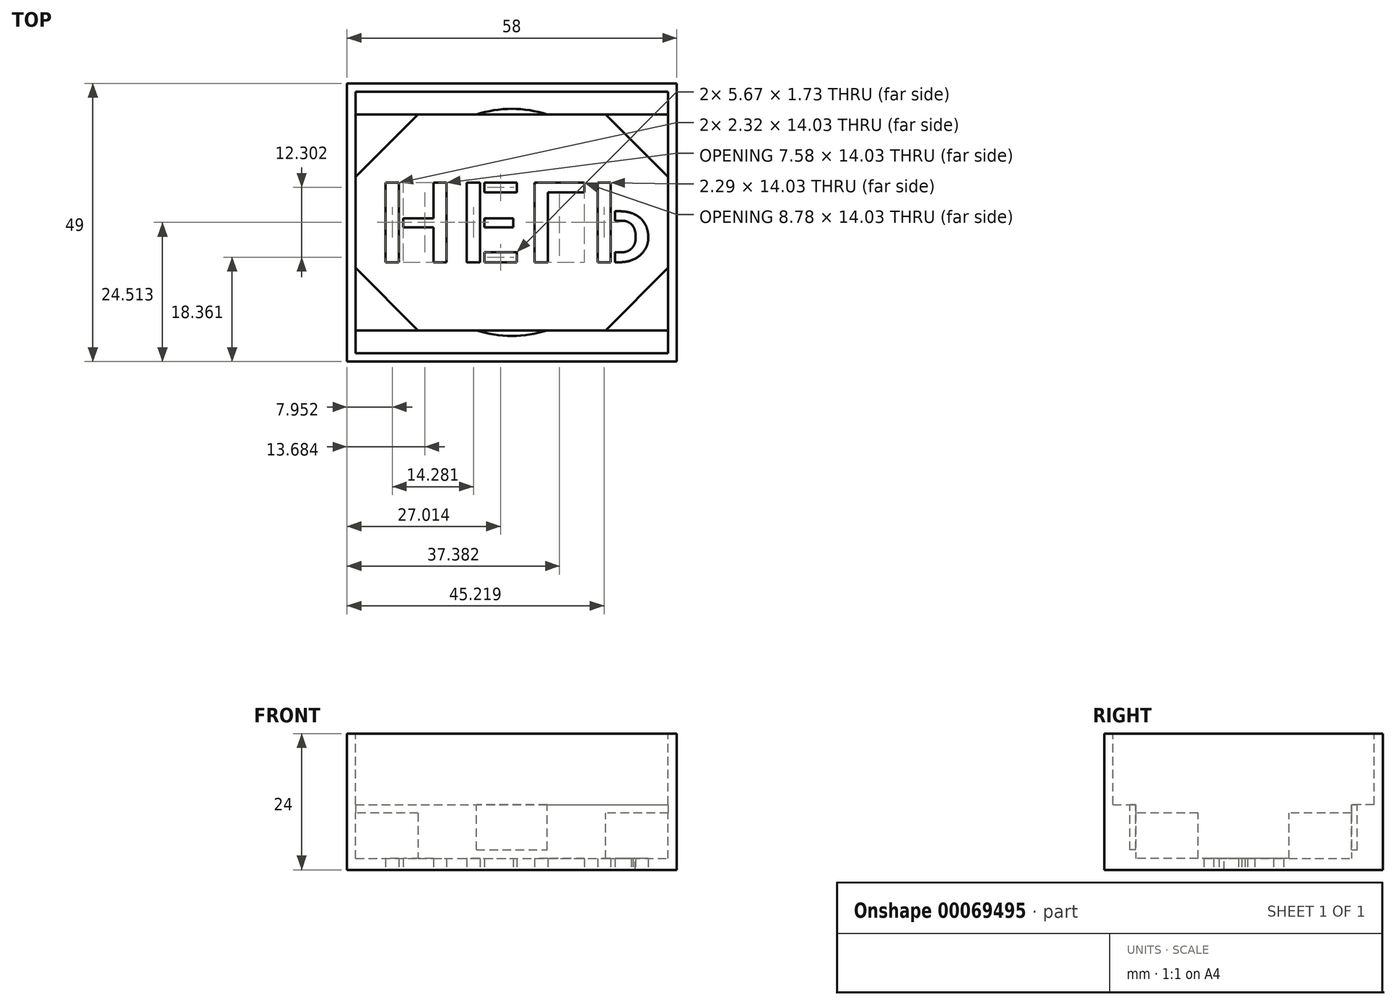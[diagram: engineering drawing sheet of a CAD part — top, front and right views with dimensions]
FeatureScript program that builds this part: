
annotation { "Feature Type Name" : "Feature", "Feature Type Description" : "" }
export const myFeature = defineFeature(function(context is Context, id is Id, definition is map)
    precondition{}
    {
        {
            var Q0;
            Q0=qCreatedBy(makeId("Top.planeOp"),FACE);
            var sketch = newSketch(context, id + "F0", { "sketchPlane" : qUnion([Q0])});
            skLineSegment(sketch, "E0.bottom", {"start": v(-21.63, 34.07) * mm, "end": v(36.37, 34.07) * mm});
            skLineSegment(sketch, "E0.top", {"start": v(-21.63, -14.93) * mm, "end": v(36.37, -14.93) * mm});
            skLineSegment(sketch, "E0.left", {"start": v(-21.63, 34.07) * mm, "end": v(-21.63, -14.93) * mm});
            skLineSegment(sketch, "E0.right", {"start": v(36.37, 34.07) * mm, "end": v(36.37, -14.93) * mm});
            skSolve(sketch);
        }
        {
            var Q0;
            Q0=makeQuery(id+"F0.imprint","IMPRINT",FACE,{"disambiguationData":[TD([[makeQuery(id+"F0.imprint","IMPRINT",EDGE,{"derivedFrom":sQuery(id+"F0.wireOp",EDGE,"E0.bottom")}),-1.0]])]});
            extrude(context, id + "F1", {"entities" : qUnion([Q0]), "depth" : 24 * mm});
        }
        {
            var Q0;
            Q0=makeQuery(id+"F1.opExtrude","CAP_FACE",FACE,{"disambiguationData":[OSD([sQuery(id+"F0.wireOp",EDGE,"E0.bottom"),sQuery(id+"F0.wireOp",EDGE,"E0.top"),sQuery(id+"F0.wireOp",EDGE,"E0.left"),sQuery(id+"F0.wireOp",EDGE,"E0.right")])],"isStart":false});
            var sketch = newSketch(context, id + "F2", { "sketchPlane" : qUnion([Q0])});
            skLineSegment(sketch, "E1.bottom", {"start": v(-20.13, 32.57) * mm, "end": v(34.87, 32.57) * mm});
            skLineSegment(sketch, "E1.top", {"start": v(-20.13, -13.43) * mm, "end": v(34.87, -13.43) * mm});
            skLineSegment(sketch, "E1.left", {"start": v(-20.13, 32.57) * mm, "end": v(-20.13, -13.43) * mm});
            skLineSegment(sketch, "E1.right", {"start": v(34.87, 32.57) * mm, "end": v(34.87, -13.43) * mm});
            skSolve(sketch);
        }
        {
            var Q0;
            Q0 = qSketchRegion(id + "F2", true);
            extrude(context, id + "F3", {"entities" : qUnion([Q0]), "operationType" : NewBodyOperationType.REMOVE, "oppositeDirection" : true, "depth" : 14 * mm});
        }
        {
            var Q0;
            Q0=makeQuery(id+"F3.boolean.opBoolean","COPY",FACE,{"derivedFrom":makeQuery(id+"F3.opExtrude","CAP_FACE",FACE,{"disambiguationData":[OSD([sQuery(id+"F2.wireOp",EDGE,"E1.bottom"),sQuery(id+"F2.wireOp",EDGE,"E1.top"),sQuery(id+"F2.wireOp",EDGE,"E1.left"),sQuery(id+"F2.wireOp",EDGE,"E1.right")])],"isStart":false})});
            var sketch = newSketch(context, id + "F4", { "sketchPlane" : qUnion([Q0])});
            skLineSegment(sketch, "E2", {"start": v(-5.13, 32.57) * mm, "end": v(-20.13, 17.57) * mm});
            skLineSegment(sketch, "E3", {"start": v(-20.13, 17.57) * mm, "end": v(-20.13, 1.57) * mm});
            skLineSegment(sketch, "E4", {"start": v(-20.13, 1.57) * mm, "end": v(-5.13, -13.43) * mm});
            skLineSegment(sketch, "E5", {"start": v(-5.13, -13.43) * mm, "end": v(19.87, -13.43) * mm});
            skLineSegment(sketch, "E6", {"start": v(19.87, -13.43) * mm, "end": v(34.87, 1.57) * mm});
            skLineSegment(sketch, "E7", {"start": v(34.87, 1.57) * mm, "end": v(34.87, 17.57) * mm});
            skLineSegment(sketch, "E8", {"start": v(34.87, 17.57) * mm, "end": v(19.87, 32.57) * mm});
            skLineSegment(sketch, "E9", {"start": v(19.87, 32.57) * mm, "end": v(-5.13, 32.57) * mm});
            skSolve(sketch);
        }
        {
            var Q0;
            Q0 = qSketchRegion(id + "F4", true);
            extrude(context, id + "F5", {"entities" : qUnion([Q0]), "operationType" : NewBodyOperationType.REMOVE, "oppositeDirection" : true, "depth" : 8 * mm});
        }
        {
            var Q0;
            Q0=makeQuery(id+"F1.opExtrude","CAP_FACE",FACE,{"disambiguationData":[OSD([sQuery(id+"F0.wireOp",EDGE,"E0.bottom"),sQuery(id+"F0.wireOp",EDGE,"E0.top"),sQuery(id+"F0.wireOp",EDGE,"E0.left"),sQuery(id+"F0.wireOp",EDGE,"E0.right")])],"isStart":true});
            var sketch = newSketch(context, id + "F6", { "sketchPlane" : qUnion([Q0])});
            skText(sketch, "E10", { "text": "HELP", "fontName": "AllertaStencil-Regular.ttf"});
            const initialGuessF6  = {"E10": [-0.01663, -0.0166, 1, 0, 0.01404]};
            skSetInitialGuess(sketch, initialGuessF6);
            skSolve(sketch);
        }
        {
            var Q0;
            Q0 = qSketchRegion(id + "F6", true);
            extrude(context, id + "F7", {"entities" : qUnion([Q0]), "operationType" : NewBodyOperationType.REMOVE, "endBound" : BoundingType.THROUGH_ALL, "oppositeDirection" : true, "depth" : 25 * mm});
        }
        {
            var Q0;
            Q0=makeQuery(id+"F5.boolean.opBoolean","COPY",FACE,{"derivedFrom":makeQuery(id+"F5.opExtrude","CAP_FACE",FACE,{"disambiguationData":[OSD([sQuery(id+"F4.wireOp",EDGE,"E2"),sQuery(id+"F4.wireOp",EDGE,"E3"),sQuery(id+"F4.wireOp",EDGE,"E4"),sQuery(id+"F4.wireOp",EDGE,"E5"),sQuery(id+"F4.wireOp",EDGE,"E6"),sQuery(id+"F4.wireOp",EDGE,"E7"),sQuery(id+"F4.wireOp",EDGE,"E8"),sQuery(id+"F4.wireOp",EDGE,"E9")])],"isStart":false})});
            var sketch = newSketch(context, id + "F8", { "sketchPlane" : qUnion([Q0])});
            skLineSegment(sketch, "E11.bottom", {"start": v(-20.13, 32.57) * mm, "end": v(34.87, 32.57) * mm});
            skLineSegment(sketch, "E11.top", {"start": v(-20.13, 28.57) * mm, "end": v(34.87, 28.57) * mm});
            skLineSegment(sketch, "E11.left", {"start": v(-20.13, 32.57) * mm, "end": v(-20.13, 28.57) * mm});
            skLineSegment(sketch, "E11.right", {"start": v(34.87, 32.57) * mm, "end": v(34.87, 28.57) * mm});
            skLineSegment(sketch, "E12.bottom", {"start": v(-20.13, -13.43) * mm, "end": v(34.87, -13.43) * mm});
            skLineSegment(sketch, "E12.top", {"start": v(-20.13, -9.43) * mm, "end": v(34.87, -9.43) * mm});
            skLineSegment(sketch, "E12.left", {"start": v(-20.13, -13.43) * mm, "end": v(-20.13, -9.43) * mm});
            skLineSegment(sketch, "E12.right", {"start": v(34.87, -13.43) * mm, "end": v(34.87, -9.43) * mm});
            skLineSegment(sketch, "E13.bottom", {"start": v(-13.63, 28.57) * mm, "end": v(-20.13, 28.57) * mm});
            skLineSegment(sketch, "E13.top", {"start": v(-13.63, -9.43) * mm, "end": v(-20.13, -9.43) * mm});
            skLineSegment(sketch, "E14.bottom", {"start": v(34.87, 28.57) * mm, "end": v(28.37, 28.57) * mm});
            skLineSegment(sketch, "E14.top", {"start": v(34.87, -9.43) * mm, "end": v(28.37, -9.43) * mm});
            skSolve(sketch);
        }
        {
            var Q0;
            Q0 = qSketchRegion(id + "F8", true);
            extrude(context, id + "F9", {"entities" : qUnion([Q0]), "operationType" : NewBodyOperationType.ADD, "depth" : 9.5 * mm});
        }
        {
            var Q0;
            Q0=makeQuery(id+"F9.opExtrude","CAP_FACE",FACE,{"disambiguationData":[OSD([sQuery(id+"F8.wireOp",EDGE,"E11.bottom"),sQuery(id+"F8.wireOp",EDGE,"E11.top"),sQuery(id+"F8.wireOp",EDGE,"E11.left"),sQuery(id+"F8.wireOp",EDGE,"E11.right"),sQuery(id+"F8.wireOp",EDGE,"E13.bottom"),sQuery(id+"F8.wireOp",EDGE,"E14.bottom")])],"isStart":false});
            var sketch = newSketch(context, id + "F10", { "sketchPlane" : qUnion([Q0])});
            skCircle(sketch, "E15", {"center": v(7.37, 9.57) * mm, "radius": 20 * mm});
            skLineSegment(sketch, "E16", {"start": v(7.37, 9.57) * mm, "end": v(-20.13, 9.57) * mm});
            skLineSegment(sketch, "E17", {"start": v(7.37, 9.57) * mm, "end": v(7.37, 28.57) * mm});
            skLineSegment(sketch, "E18", {"start": v(7.37, 9.57) * mm, "end": v(34.87, 9.57) * mm});
            skPoint(sketch, "E18.endSnap0", {"position": v(34.87, 9.57) * mm});
            skLineSegment(sketch, "E19", {"start": v(7.37, 9.57) * mm, "end": v(7.37, -9.43) * mm});
            skSolve(sketch);
        }
        {
            var Q0;
            Q0 = qSketchRegion(id + "F10", true);
            extrude(context, id + "F11", {"entities" : qUnion([Q0]), "operationType" : NewBodyOperationType.REMOVE, "oppositeDirection" : true, "depth" : 8 * mm});
        }
    });
